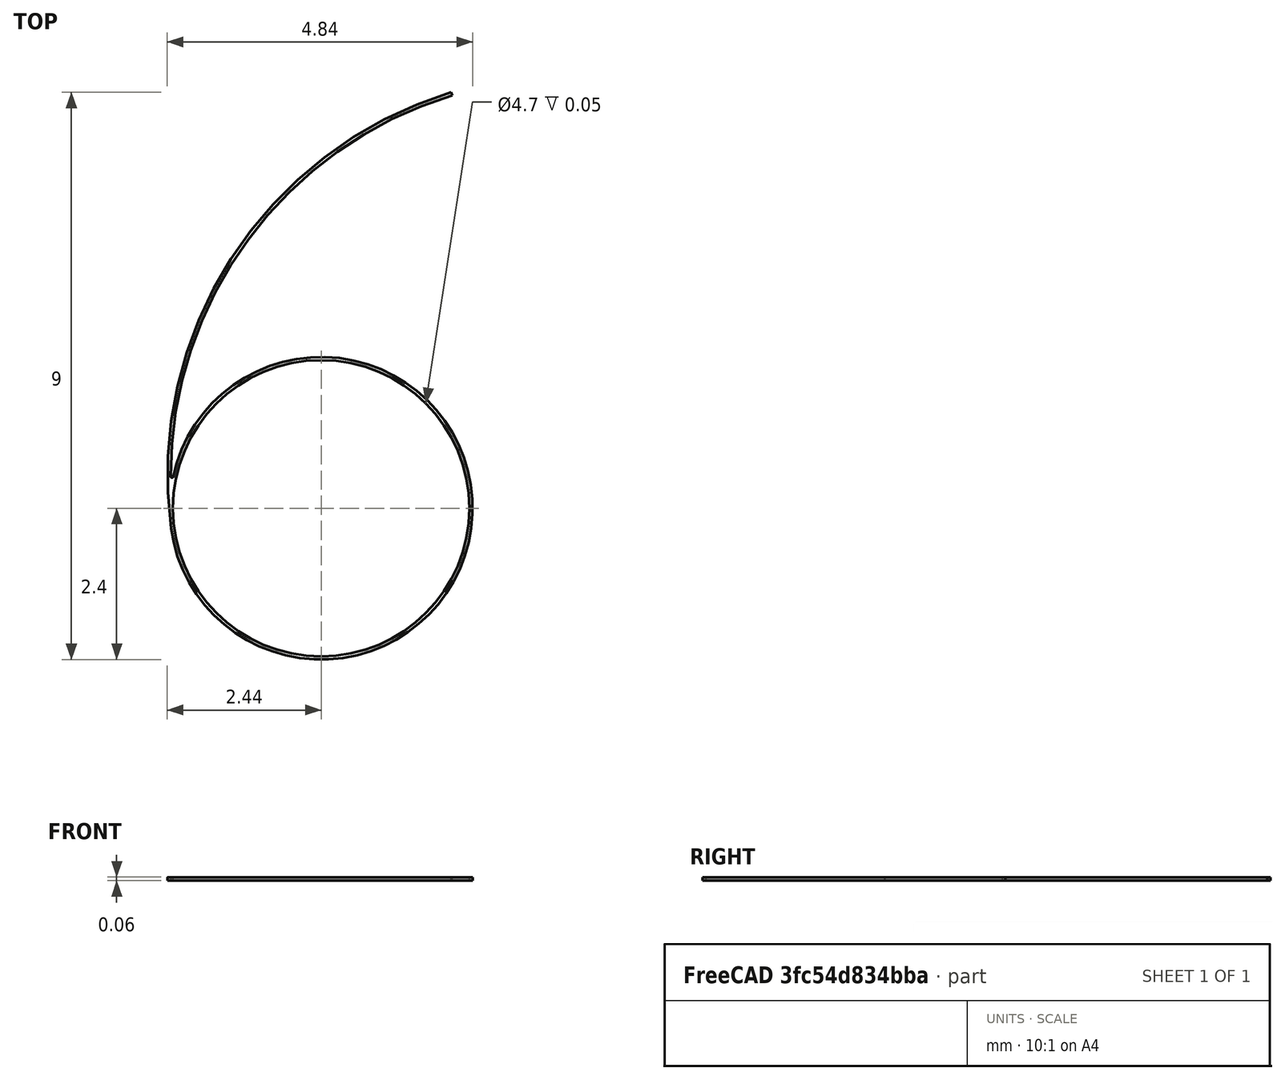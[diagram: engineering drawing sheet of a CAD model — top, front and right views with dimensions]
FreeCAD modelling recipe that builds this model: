
FCSTD DOCUMENT  (FreeCAD 0.16R6712 (Git))
Label: 6t
License: All rights reserved
LicenseURL: http://en.wikipedia.org/wiki/All_rights_reserved
objects: Sketcher::SketchObject×1, PartDesign::Pad×1, Mesh::Feature×1
note: 3 computed .brp shape members not serialized (recipe doc carries the construction recipe); baked Part::Feature solids carry a one-line shape summary decoded from their .brp

FEATURE [Sketcher::SketchObject] Sketch
  sketch-geometry (6):
    g0: ArcOfCircle CenterX=3.91093 CenterY=2.92861 CenterZ=0 NormalX=0 NormalY=0 NormalZ=1 Radius=6.3465 StartAngle=1.86631 EndAngle=3.27594
    g1: ArcOfCircle CenterX=-2.36551 CenterY=2.90352 CenterZ=0 NormalX=0 NormalY=0 NormalZ=1 Radius=0.02 StartAngle=3.14566 EndAngle=5.68649
    g2: ArcOfCircle CenterX=0 CenterY=2.4 CenterZ=0 NormalX=0 NormalY=0 NormalZ=1 Radius=2.4 StartAngle=3.27594 EndAngle=9.21819
    g3: ArcOfCircle CenterX=3.91093 CenterY=2.92861 CenterZ=0 NormalX=0 NormalY=0 NormalZ=1 Radius=6.2965 StartAngle=1.86631 EndAngle=3.14559
    g4: LineSegment StartX=2.06261 StartY=9 StartZ=0 EndX=2.07717 EndY=8.95217 EndZ=0
    g5: Circle CenterX=0 CenterY=2.4 CenterZ=0 NormalX=0 NormalY=0 NormalZ=1 Radius=2.35
  constraints (16):
    c: Tangent(g0,g2) = -1.5708
    c: Radius(g2) = 2.4
    c: PointOnObject(g2,g-2)
    c: Coincident(g2,g1)
    c: Coincident(g1,g3)
    c: Tangent(g1,g3)
    c: Coincident(g4,g0)
    c: Coincident(g4,g3)
    c: Radius(g1) = 0.02
    c: PointOnObject(g-1,g2)
    c: Radius(g5) = 2.35
    c: Coincident(g2,g5)
    c: DistanceY(g-1,g0) = 9
    c: Coincident(g0,g3)
    c: Perpendicular(g3,g4)
    c: Distance(g3,g0) = 0.05
FEATURE [PartDesign::Pad] Pad
  Length = 0.05
  Length2 = 100
  Midplane = true
  Sketch = -> Sketch
  Type = 0
FEATURE [Mesh::Feature] Mesh  label="Pad (Meshed)"
